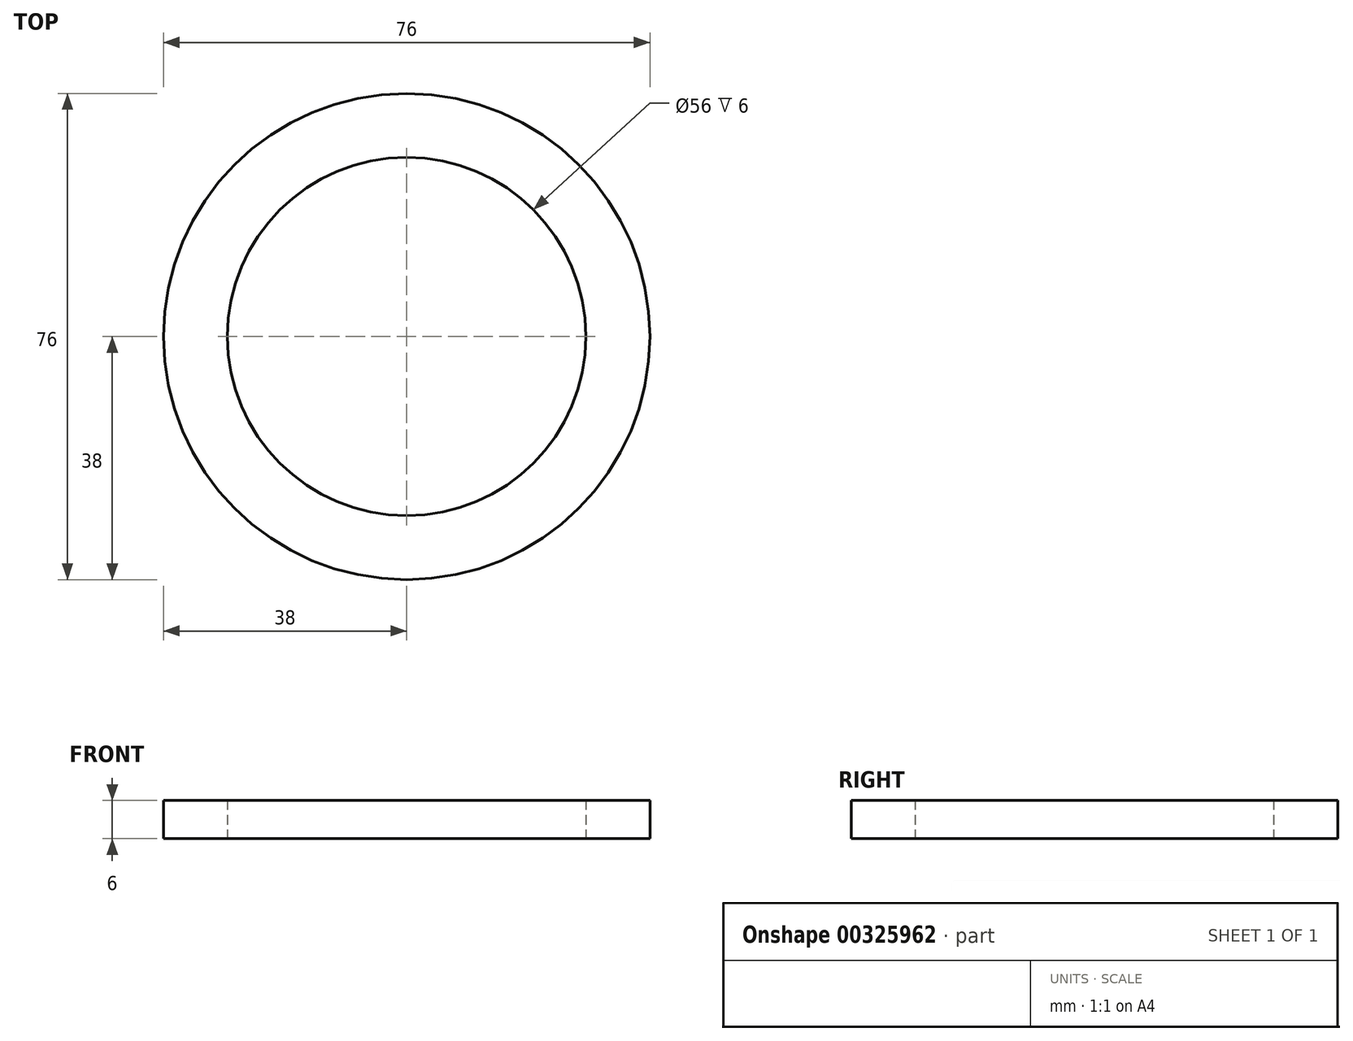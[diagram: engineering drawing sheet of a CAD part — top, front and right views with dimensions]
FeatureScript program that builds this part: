
annotation { "Feature Type Name" : "Feature", "Feature Type Description" : "" }
export const myFeature = defineFeature(function(context is Context, id is Id, definition is map)
    precondition{}
    {
        {
            var Q0;
            Q0=qCreatedBy(makeId("Top.planeOp"),FACE);
            var sketch = newSketch(context, id + "F0", { "sketchPlane" : qUnion([Q0])});
            skCircle(sketch, "E0", {"center": v(0, 0) * mm, "radius": 28 * mm});
            skCircle(sketch, "E1.0", {"center": v(0, 0) * mm, "radius": 38 * mm});
            skSolve(sketch);
        }
        {
            var Q0;
            Q0 = qSketchRegion(id + "F0", true);
            extrude(context, id + "F1", {"entities" : qUnion([Q0]), "depth" : 6 * mm});
        }
    });
